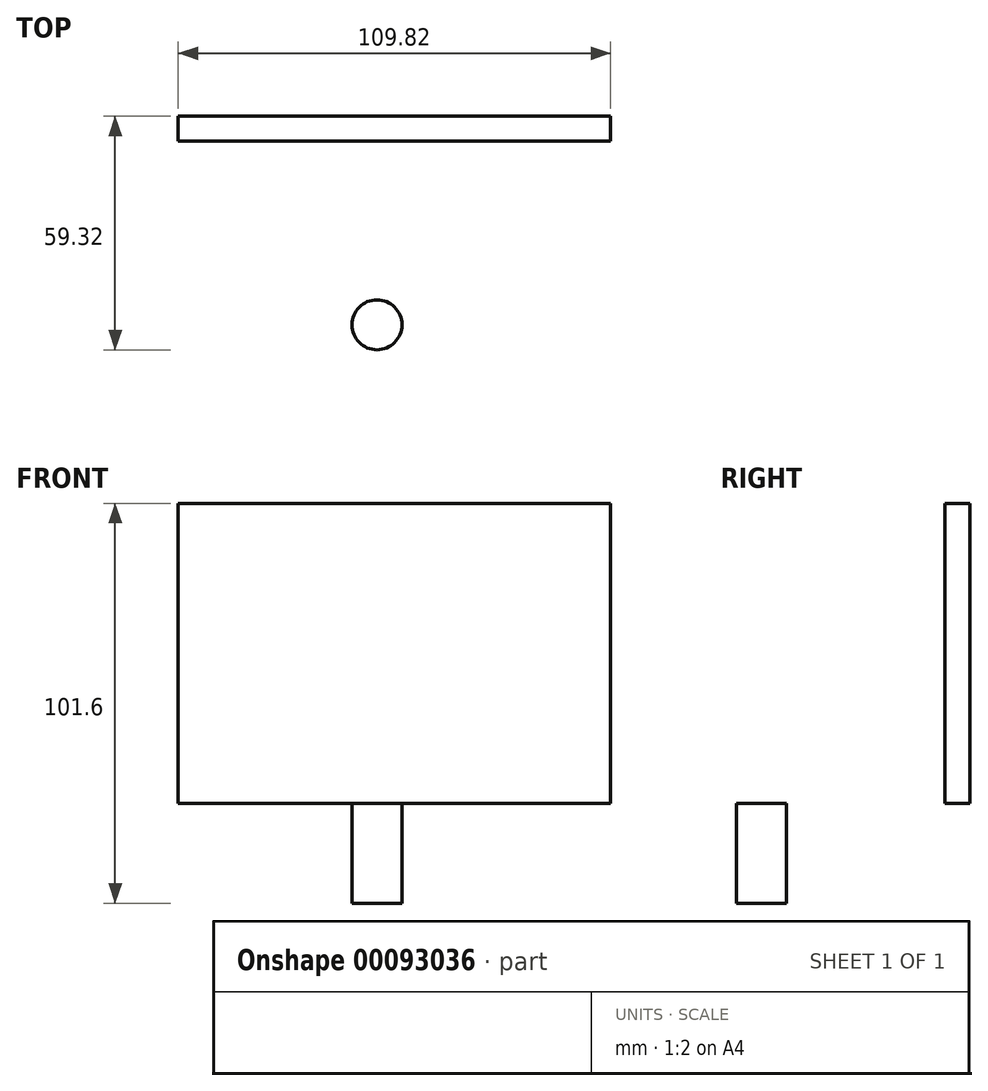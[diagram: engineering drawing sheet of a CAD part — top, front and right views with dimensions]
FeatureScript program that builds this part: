
annotation { "Feature Type Name" : "Feature", "Feature Type Description" : "" }
export const myFeature = defineFeature(function(context is Context, id is Id, definition is map)
    precondition{}
    {
        {
            var Q0;
            Q0=qCreatedBy(makeId("Front.planeOp"),FACE);
            var sketch = newSketch(context, id + "F0", { "sketchPlane" : qUnion([Q0])});
            skLineSegment(sketch, "E0.bottom", {"start": v(-50.49, 44.97) * mm, "end": v(59.33, 44.97) * mm});
            skLineSegment(sketch, "E0.top", {"start": v(-50.49, -31.23) * mm, "end": v(59.33, -31.23) * mm});
            skLineSegment(sketch, "E0.left", {"start": v(-50.49, 44.97) * mm, "end": v(-50.49, -31.23) * mm});
            skLineSegment(sketch, "E0.right", {"start": v(59.33, 44.97) * mm, "end": v(59.33, -31.23) * mm});
            skSolve(sketch);
        }
        {
            var Q0;
            Q0=makeQuery(id+"F0.imprint","IMPRINT",FACE,{"disambiguationData":[TD([[makeQuery(id+"F0.imprint","IMPRINT",EDGE,{"derivedFrom":sQuery(id+"F0.wireOp",EDGE,"E0.bottom")}),-1.0]])]});
            extrude(context, id + "F1", {"entities" : qUnion([Q0]), "depth" : 6.35 * mm});
        }
        {
            var Q0;
            Q0=makeQuery(id+"F1.opExtrude","SWEPT_FACE",FACE,{"disambiguationData":[OSD([sQuery(id+"F0.wireOp",EDGE,"E0.top")])]});
            var sketch = newSketch(context, id + "F2", { "sketchPlane" : qUnion([Q0])});
            skCircle(sketch, "E1", {"center": v(0, 52.97) * mm, "radius": 6.35 * mm});
            skLineSegment(sketch, "E2", {"start": v(-34.25, 6.35) * mm, "end": v(-5.5, 56.14) * mm});
            skLineSegment(sketch, "E3", {"start": v(5.5, 56.14) * mm, "end": v(34.25, 6.35) * mm});
            skPoint(sketch, "E4.orphan", {"position": v(0, 65.67) * mm});
            skSolve(sketch);
        }
        {
            var Q0;
            Q0=makeQuery(id+"F2.imprint","IMPRINT",FACE,{"disambiguationData":[TD([[makeQuery(id+"F2.imprint","IMPRINT",EDGE,{"derivedFrom":sQuery(id+"F2.wireOp",EDGE,"E1")}),1.0]])]});
            extrude(context, id + "F3", {"entities" : qUnion([Q0]), "depth" : 25.4 * mm});
        }
    });
